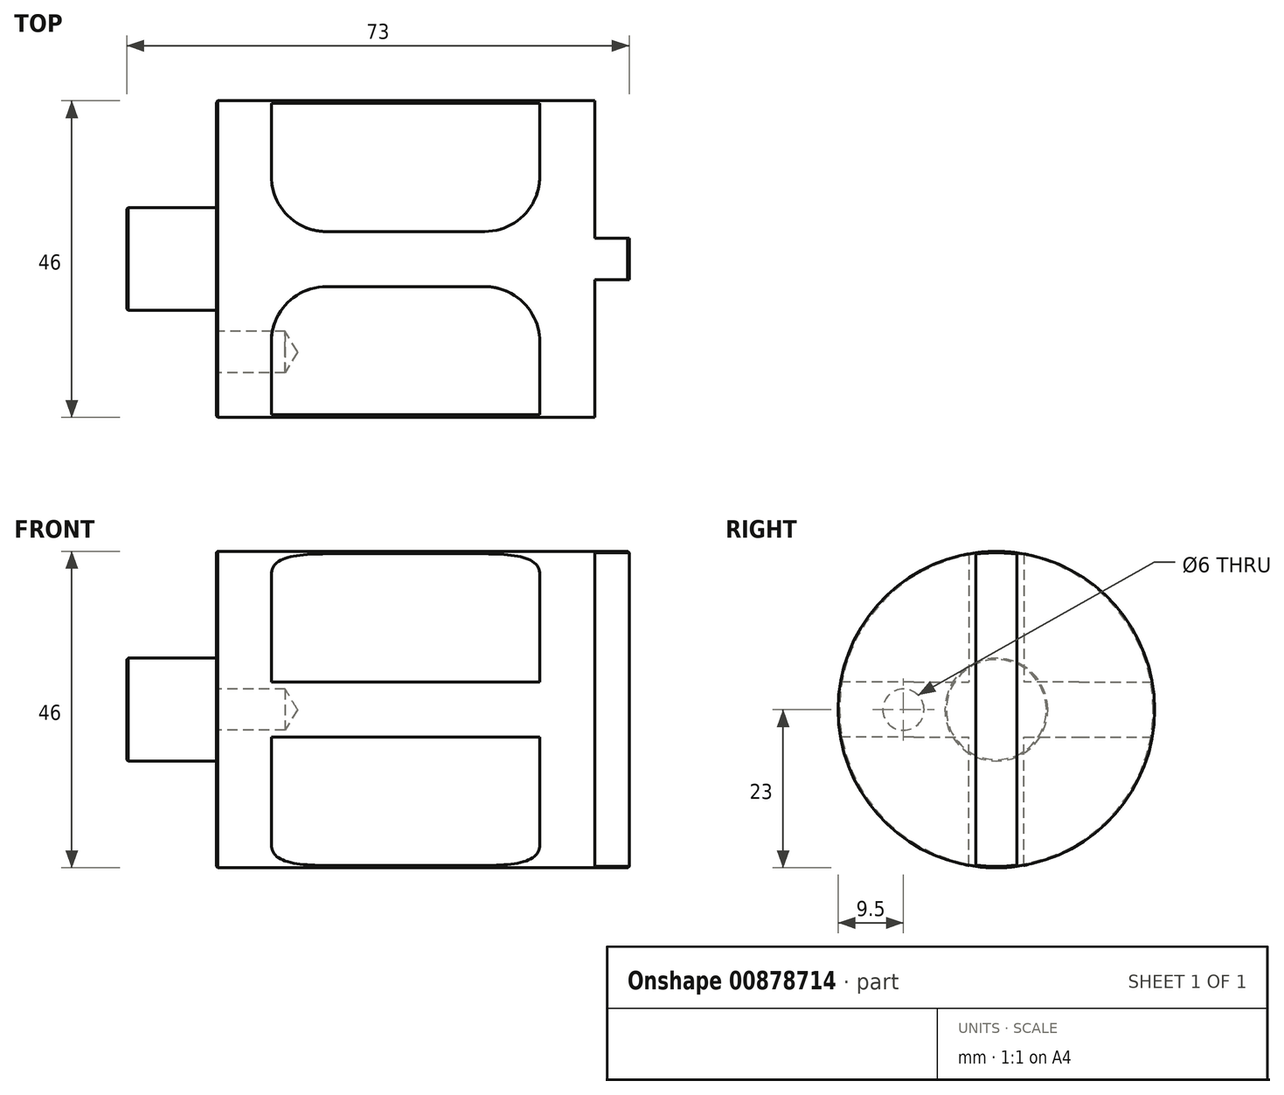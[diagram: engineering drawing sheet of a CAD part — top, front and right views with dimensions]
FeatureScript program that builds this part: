
annotation { "Feature Type Name" : "Feature", "Feature Type Description" : "" }
export const myFeature = defineFeature(function(context is Context, id is Id, definition is map)
    precondition{}
    {
        {
            var Q0;
            Q0=qCreatedBy(makeId("Front.planeOp"),FACE);
            var sketch = newSketch(context, id + "F0", { "sketchPlane" : qUnion([Q0])});
            skLineSegment(sketch, "E0", {"start": v(-29.08, 0) * mm, "end": v(-29.08, 7.47) * mm});
            skLineSegment(sketch, "E1", {"start": v(-29.08, 7.47) * mm, "end": v(-16.08, 7.47) * mm});
            skLineSegment(sketch, "E2", {"start": v(-16.08, 7.47) * mm, "end": v(-16.08, 23) * mm});
            skLineSegment(sketch, "E3", {"start": v(-16.08, 23) * mm, "end": v(43.92, 23) * mm});
            skLineSegment(sketch, "E4", {"start": v(43.92, 23) * mm, "end": v(43.92, 0) * mm});
            skLineSegment(sketch, "E5", {"start": v(-37.08, 0) * mm, "end": v(49.94, 0) * mm});
            skSolve(sketch);
        }
        {
            var Q0;
            {var subQ0=sQuery(id+"F0.wireOp",EDGE,"E0");Q0=makeQuery(id+"F0.imprint","IMPRINT",FACE,{"disambiguationData":[TD([[makeQuery(id+"F0.imprint","IMPRINT",EDGE,{"derivedFrom":subQ0}),-1.0]])]});}
            var Q1;
            Q1=sQuery(id+"F0.wireOp",EDGE,"E5");
            revolve(context, id + "F1", {"surfaceOperationType" : NewSurfaceOperationType.NEW, "entities" : qUnion([Q0]), "axis" : qUnion([Q1]), "revolveType" : RevolveType.FULL});
        }
        {
            var Q0;
            Q0=makeQuery(id+"F1.opRevolve","SWEPT_FACE",FACE,{"disambiguationData":[OSD([sQuery(id+"F0.wireOp",EDGE,"E4")])]});
            var sketch = newSketch(context, id + "F2", { "sketchPlane" : qUnion([Q0])});
            skLineSegment(sketch, "E6.left", {"start": v(-3, 25) * mm, "end": v(-3, -25) * mm});
            skLineSegment(sketch, "E6.right", {"start": v(3, 25) * mm, "end": v(3, -25) * mm});
            skPoint(sketch, "E6.middle", {"position": v(0, 0) * mm});
            skArc(sketch, "E7", {"start": v(-3, 25) * mm, "mid": v(-25.18, 0) * mm, "end": v(-3, -25) * mm});
            skArc(sketch, "E8.trimOffspring", {"start": v(3, -25) * mm, "mid": v(25.18, 0) * mm, "end": v(3, 25) * mm});
            skSolve(sketch);
        }
        {
            var Q0;
            {var subQ0=sQuery(id+"F2.wireOp",EDGE,"E6.left");var subQ1=makeQuery(id+"F1.opRevolve","SWEPT_EDGE",EDGE,{"disambiguationData":[OSD([sQuery(id+"F0.wireOp",EDGE,"E3"),sQuery(id+"F0.wireOp",EDGE,"E4")])]});var subQ2=makeQuery(id+"F2.imprint","INTERSECT",VERTEX,{"disambiguationData":[OD(0.0)],"derivedFrom":[subQ1,subQ0]});Q0=makeQuery(id+"F2.imprint","IMPRINT",FACE,{"disambiguationData":[TD([[makeQuery(id+"F2.imprint","IMPRINT",EDGE,{"disambiguationData":[TD([[subQ2,-1.0]])],"derivedFrom":subQ0}),-1.0]])]});}
            var Q1;
            {var subQ0=sQuery(id+"F2.wireOp",EDGE,"E6.right");var subQ1=makeQuery(id+"F1.opRevolve","SWEPT_EDGE",EDGE,{"disambiguationData":[OSD([sQuery(id+"F0.wireOp",EDGE,"E3"),sQuery(id+"F0.wireOp",EDGE,"E4")])]});var subQ2=makeQuery(id+"F2.imprint","INTERSECT",VERTEX,{"disambiguationData":[OD(0.0)],"derivedFrom":[subQ1,subQ0]});Q1=makeQuery(id+"F2.imprint","IMPRINT",FACE,{"disambiguationData":[TD([[makeQuery(id+"F2.imprint","IMPRINT",EDGE,{"disambiguationData":[TD([[subQ2,-1.0]])],"derivedFrom":subQ0}),1.0]])]});}
            extrude(context, id + "F3", {"entities" : qUnion([Q0, Q1]), "operationType" : NewBodyOperationType.REMOVE, "oppositeDirection" : true, "depth" : 5 * mm, "offsetDistance" : 25 * mm});
        }
        {
            var Q0;
            Q0=qCreatedBy(makeId("Top.planeOp"),FACE);
            cPlane(context, id + "F4", {"entities" : qUnion([Q0]), "cplaneType" : CPlaneType.OFFSET, "offset" : 4 * mm, "width" : 150 * mm, "height" : 150 * mm});
        }
        {
            var Q0;
            Q0=qCreatedBy(makeId("Top.planeOp"),FACE);
            cPlane(context, id + "F5", {"entities" : qUnion([Q0]), "cplaneType" : CPlaneType.OFFSET, "offset" : 4 * mm, "oppositeDirection" : true, "width" : 150 * mm, "height" : 150 * mm});
        }
        {
            var Q0;
            Q0=qCreatedBy(id+"F4.planeOp",FACE);
            var sketch = newSketch(context, id + "F6", { "sketchPlane" : qUnion([Q0])});
            skLineSegment(sketch, "E9.bottom", {"start": v(-8.08, 4) * mm, "end": v(30.92, 4) * mm});
            skLineSegment(sketch, "E9.top", {"start": v(-8.08, 25.88) * mm, "end": v(30.92, 25.88) * mm});
            skLineSegment(sketch, "E9.left", {"start": v(-8.08, 4) * mm, "end": v(-8.08, 25.88) * mm});
            skLineSegment(sketch, "E9.right", {"start": v(30.92, 4) * mm, "end": v(30.92, 25.88) * mm});
            skLineSegment(sketch, "E10.bottom", {"start": v(-8.08, -4) * mm, "end": v(30.92, -4) * mm});
            skLineSegment(sketch, "E10.top", {"start": v(-8.08, -25.98) * mm, "end": v(30.92, -25.98) * mm});
            skLineSegment(sketch, "E10.left", {"start": v(-8.08, -4) * mm, "end": v(-8.08, -25.98) * mm});
            skLineSegment(sketch, "E10.right", {"start": v(30.92, -4) * mm, "end": v(30.92, -25.98) * mm});
            skSolve(sketch);
        }
        {
            var Q0;
            Q0=makeQuery(id+"F6.imprint","IMPRINT",FACE,{"disambiguationData":[TD([[makeQuery(id+"F6.imprint","IMPRINT",EDGE,{"derivedFrom":sQuery(id+"F6.wireOp",EDGE,"E9.bottom")}),1.0]])]});
            var Q1;
            Q1=makeQuery(id+"F6.imprint","IMPRINT",FACE,{"disambiguationData":[TD([[makeQuery(id+"F6.imprint","IMPRINT",EDGE,{"derivedFrom":sQuery(id+"F6.wireOp",EDGE,"E10.bottom")}),-1.0]])]});
            extrude(context, id + "F7", {"entities" : qUnion([Q0, Q1]), "operationType" : NewBodyOperationType.REMOVE, "endBound" : BoundingType.UP_TO_NEXT, "depth" : 25 * mm, "offsetDistance" : 25 * mm});
        }
        {
            var Q0;
            Q0=qCreatedBy(id+"F5.planeOp",FACE);
            var sketch = newSketch(context, id + "F8", { "sketchPlane" : qUnion([Q0])});
            skLineSegment(sketch, "E11.bottom", {"start": v(-8.08, -4) * mm, "end": v(30.92, -4) * mm});
            skLineSegment(sketch, "E11.top", {"start": v(-8.08, -34.98) * mm, "end": v(30.92, -34.98) * mm});
            skLineSegment(sketch, "E11.left", {"start": v(-8.08, -4) * mm, "end": v(-8.08, -34.98) * mm});
            skLineSegment(sketch, "E11.right", {"start": v(30.92, -4) * mm, "end": v(30.92, -34.98) * mm});
            skLineSegment(sketch, "E12.bottom", {"start": v(-8.08, 4) * mm, "end": v(30.92, 4) * mm});
            skLineSegment(sketch, "E12.top", {"start": v(-8.08, 31.39) * mm, "end": v(30.92, 31.39) * mm});
            skLineSegment(sketch, "E12.left", {"start": v(-8.08, 4) * mm, "end": v(-8.08, 31.39) * mm});
            skLineSegment(sketch, "E12.right", {"start": v(30.92, 4) * mm, "end": v(30.92, 31.39) * mm});
            skSolve(sketch);
        }
        {
            var Q0;
            Q0=makeQuery(id+"F8.imprint","IMPRINT",FACE,{"disambiguationData":[TD([[makeQuery(id+"F8.imprint","IMPRINT",EDGE,{"derivedFrom":sQuery(id+"F8.wireOp",EDGE,"E11.bottom")}),-1.0]])]});
            var Q1;
            Q1=makeQuery(id+"F8.imprint","IMPRINT",FACE,{"disambiguationData":[TD([[makeQuery(id+"F8.imprint","IMPRINT",EDGE,{"derivedFrom":sQuery(id+"F8.wireOp",EDGE,"E12.bottom")}),1.0]])]});
            extrude(context, id + "F9", {"entities" : qUnion([Q0, Q1]), "operationType" : NewBodyOperationType.REMOVE, "endBound" : BoundingType.UP_TO_NEXT, "oppositeDirection" : true, "depth" : 25 * mm, "offsetDistance" : 25 * mm});
        }
        {
            var Q0;
            Q0=makeQuery(id+"F1.opRevolve","SWEPT_FACE",FACE,{"disambiguationData":[OSD([sQuery(id+"F0.wireOp",EDGE,"E2")])]});
            var sketch = newSketch(context, id + "F10", { "sketchPlane" : qUnion([Q0])});
            skPoint(sketch, "E13", {"position": v(13.5, 0) * mm});
            skSolve(sketch);
        }
        {
            var Q0;
            Q0=sQuery(id+"F10.wireOp",VERTEX,"E13");
            var Q1;
            Q1=makeQuery(id+"F1.opRevolve","SWEPT_BODY",BODY,{"disambiguationData":[OSD([sQuery(id+"F0.wireOp",EDGE,"E0"),sQuery(id+"F0.wireOp",EDGE,"E1"),sQuery(id+"F0.wireOp",EDGE,"E2"),sQuery(id+"F0.wireOp",EDGE,"E3"),sQuery(id+"F0.wireOp",EDGE,"E4"),sQuery(id+"F0.wireOp",EDGE,"E5")])]});
            hole(context, id + "F11", {"style" : HoleStyle.SIMPLE, "endStyle" : HoleEndStyle.BLIND, "standardTappedOrClearance" : lookupTablePath({ "standard" : "ISO", "size" : "6", "type" : "Drilled" }), "standardBlindInLast" : lookupTablePath({ "standard" : "ISO", "size" : "6", "type" : "Drilled" }), "holeDiameter" : 6 * mm, "majorDiameter" : 5 * mm, "holeDepth" : 10 * mm, "isTappedThrough" : true, "tappedDepth" : 12 * mm, "tapClearance" : 3, "startFromSketch" : true, "locations" : qUnion([Q0]), "scope" : qUnion([Q1])});
        }
        {
            var Q0;
            Q0=makeQuery(id+"F1.opRevolve","SWEPT_EDGE",EDGE,{"disambiguationData":[OSD([sQuery(id+"F0.wireOp",EDGE,"E2"),sQuery(id+"F0.wireOp",EDGE,"E3")])]});
            var Q1;
            {var subQ0=sQuery(id+"F2.wireOp",EDGE,"E6.right");var subQ1=sQuery(id+"F0.wireOp",EDGE,"E4");var subQ2=sQuery(id+"F0.wireOp",EDGE,"E3");var subQ3=makeQuery(id+"F1.opRevolve","SWEPT_EDGE",EDGE,{"disambiguationData":[OSD([subQ2,subQ1])]});Q1=makeQuery(id+"F3.boolean.opBoolean","COPY",EDGE,{"derivedFrom":makeQuery(id+"F3.opExtrude","CAP_EDGE",EDGE,{"disambiguationData":[OSD([subQ2,subQ1]),TDD([makeQuery(id+"F2.imprint","IMPRINT",EDGE,{"disambiguationData":[TD([[makeQuery(id+"F2.imprint","INTERSECT",VERTEX,{"disambiguationData":[OD(0.0)],"derivedFrom":[subQ3,subQ0]}),-1.0]])],"derivedFrom":subQ3})])],"isStart":false})});}
            var Q2;
            {var subQ0=sQuery(id+"F2.wireOp",EDGE,"E6.left");var subQ1=sQuery(id+"F0.wireOp",EDGE,"E4");var subQ2=sQuery(id+"F0.wireOp",EDGE,"E3");var subQ3=makeQuery(id+"F1.opRevolve","SWEPT_EDGE",EDGE,{"disambiguationData":[OSD([subQ2,subQ1])]});Q2=makeQuery(id+"F3.boolean.opBoolean","COPY",EDGE,{"derivedFrom":makeQuery(id+"F3.opExtrude","CAP_EDGE",EDGE,{"disambiguationData":[OSD([subQ2,subQ1]),TDD([makeQuery(id+"F2.imprint","IMPRINT",EDGE,{"disambiguationData":[TD([[makeQuery(id+"F2.imprint","INTERSECT",VERTEX,{"disambiguationData":[OD(0.0)],"derivedFrom":[subQ3,subQ0]}),1.0]])],"derivedFrom":subQ3})])],"isStart":false})});}
            var Q3;
            Q3=makeQuery(id+"F3.boolean.opBoolean","SPLIT",EDGE,{"disambiguationData":[OD(1.0)],"derivedFrom":makeQuery(id+"F1.opRevolve","SWEPT_EDGE",EDGE,{"disambiguationData":[OSD([sQuery(id+"F0.wireOp",EDGE,"E3"),sQuery(id+"F0.wireOp",EDGE,"E4")])]})});
            var Q4;
            Q4=makeQuery(id+"F3.boolean.opBoolean","SPLIT",EDGE,{"disambiguationData":[OD(0.0)],"derivedFrom":makeQuery(id+"F1.opRevolve","SWEPT_EDGE",EDGE,{"disambiguationData":[OSD([sQuery(id+"F0.wireOp",EDGE,"E3"),sQuery(id+"F0.wireOp",EDGE,"E4")])]})});
            var Q5;
            Q5=makeQuery(id+"F1.opRevolve","SWEPT_EDGE",EDGE,{"disambiguationData":[OSD([sQuery(id+"F0.wireOp",EDGE,"E0"),sQuery(id+"F0.wireOp",EDGE,"E1")])]});
            chamfer(context, id + "F12", {"entities" : qUnion([Q0, Q1, Q2, Q3, Q4, Q5]), "width" : 0.2 * mm, "tangentPropagation" : true});
        }
        {
            var Q0;
            Q0=makeQuery(id+"F7.boolean.opBoolean","COPY",EDGE,{"derivedFrom":makeQuery(id+"F7.opExtrude","SWEPT_EDGE",EDGE,{"disambiguationData":[OSD([sQuery(id+"F6.wireOp",EDGE,"E10.bottom"),sQuery(id+"F6.wireOp",EDGE,"E10.left")])]})});
            var Q1;
            Q1=makeQuery(id+"F7.boolean.opBoolean","COPY",EDGE,{"derivedFrom":makeQuery(id+"F7.opExtrude","SWEPT_EDGE",EDGE,{"disambiguationData":[OSD([sQuery(id+"F6.wireOp",EDGE,"E10.bottom"),sQuery(id+"F6.wireOp",EDGE,"E10.right")])]})});
            var Q2;
            Q2=makeQuery(id+"F7.boolean.opBoolean","COPY",EDGE,{"derivedFrom":makeQuery(id+"F7.opExtrude","SWEPT_EDGE",EDGE,{"disambiguationData":[OSD([sQuery(id+"F6.wireOp",EDGE,"E9.bottom"),sQuery(id+"F6.wireOp",EDGE,"E9.right")])]})});
            var Q3;
            Q3=makeQuery(id+"F7.boolean.opBoolean","COPY",EDGE,{"derivedFrom":makeQuery(id+"F7.opExtrude","SWEPT_EDGE",EDGE,{"disambiguationData":[OSD([sQuery(id+"F6.wireOp",EDGE,"E9.bottom"),sQuery(id+"F6.wireOp",EDGE,"E9.left")])]})});
            var Q4;
            Q4=makeQuery(id+"F9.boolean.opBoolean","COPY",EDGE,{"derivedFrom":makeQuery(id+"F9.opExtrude","SWEPT_EDGE",EDGE,{"disambiguationData":[OSD([sQuery(id+"F8.wireOp",EDGE,"E11.bottom"),sQuery(id+"F8.wireOp",EDGE,"E11.left")])]})});
            var Q5;
            Q5=makeQuery(id+"F9.boolean.opBoolean","COPY",EDGE,{"derivedFrom":makeQuery(id+"F9.opExtrude","SWEPT_EDGE",EDGE,{"disambiguationData":[OSD([sQuery(id+"F8.wireOp",EDGE,"E11.bottom"),sQuery(id+"F8.wireOp",EDGE,"E11.right")])]})});
            var Q6;
            Q6=makeQuery(id+"F9.boolean.opBoolean","COPY",EDGE,{"derivedFrom":makeQuery(id+"F9.opExtrude","SWEPT_EDGE",EDGE,{"disambiguationData":[OSD([sQuery(id+"F8.wireOp",EDGE,"E12.bottom"),sQuery(id+"F8.wireOp",EDGE,"E12.left")])]})});
            var Q7;
            Q7=makeQuery(id+"F9.boolean.opBoolean","COPY",EDGE,{"derivedFrom":makeQuery(id+"F9.opExtrude","SWEPT_EDGE",EDGE,{"disambiguationData":[OSD([sQuery(id+"F8.wireOp",EDGE,"E12.bottom"),sQuery(id+"F8.wireOp",EDGE,"E12.right")])]})});
            fillet(context, id + "F13", {"entities" : qUnion([Q0, Q1, Q2, Q3, Q4, Q5, Q6, Q7]), "radius" : 8 * mm, "tangentPropagation" : true, "allowEdgeOverflow" : false});
        }
    });
